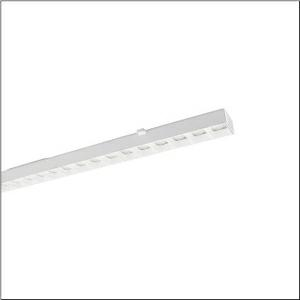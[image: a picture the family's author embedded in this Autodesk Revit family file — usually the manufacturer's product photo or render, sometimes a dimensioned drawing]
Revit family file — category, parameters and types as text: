
# Revit family: silica_r__31_fur_modario_r__31_51ry1tmb46c_60a4
name_source: partatom
category: Lighting Fixtures
units: mm (PartAtom-declared; Revit-internal decimal feet)

## family parameters
Cut with Voids When Loaded = No
Host = Face
Light Source = No
Part Type = Normal
Room Calculation Point = No
Round Connector Dimension = Use Diameter
Shared = No

## types (1)
- --- (1 x LED, 6710 lm, 37.8 W, 4000K)
    Apparent Load = 38 VA
    CIE Flux Codes = 84 98 100 100 100
    Color Rendering = 80
    Color Temperature = 4000K
    Default Elevation = 1800 mm
    Description = Silica® 31 for Modario® 31, luminaire insert, of aluminium, coated, traffic white (RAL 9016), length: 1.495mm, width: 79mm, height: 62mm, 5x system unit, system units: 299mm, LED rated luminous flux: 6.710lm, light colour: 840, control gear: ON/OFF Multilumen, with system connector: socket, mains connection: 220..240V, AC, 50/60Hz, rated input power: 38W, luminous flux adjustable on luminaire in four steps (3920/4730/5690/6710lm), connected load according to luminous flux setting (21.7/26.2/31.8/37.8W), primary light control with lens, of PMMA, primary anti-glare with reflector, of PC, CAT 2 (L<= 3000cd/m²), light emission: direct distribution, primary light characteristic: symmetric, protection rating (complete): IP20, insulation class (complete): insulation class I (protective earthing), certification: CE, UKCA, impact resistance: IK02, permissible ambient temperature for indoor applications: -20..+40°C, packaging unit: 1 piece
    Height = 62 mm  [stored 0.203412 ft]
    Lamp = 1 x LED
    Lamp Light Flux = 6710 lm
    Lamp Power = 37.8 W
    Lamp count = 1
    Length = 1495 mm
    Luminous efficacy = 178 lm/W
    Manufacturer = Siteco
    ModVariant = No
    Model = 51RY1TMB46C
    Mounting Place = Ceiling
    Mounting Type = Pendant
    Number of Poles = 1
    OnlyDefault = Yes
    Power Factor = 1
    Product Name = Silica® 31 für Modario® 31
    Product group = luminaire insert | ceiling pendant
    ProductGroupID = 902
    Protection Class = Protection class I
    Protection Degree = IP 20
    RLX_Detail_Level = 1
    RLX_Emergency_Light_Flux = 0 lm
    RLX_Emergency_Type = 0
    RLX_Emergency_Type_DB = No
    RlxData = <blob elided: 14069 chars, md5=0acf7f24>
    Socket = socket
    Standby Power = 0 W
    System Light Flux = 6710 lm
    System Power = 38 W
    Type Comments = factory setting: luminous flux: 100 % | (OFF | OFF | OFF) | 350 mA
    Type Image = l_1299352.jpg
    URL = http://relux.com
    VarID = @adj_078295
    Voltage = 0 V
    Weight = 0.00 kg
    Width = 79 mm

note: [stored X ft] marks values corroborated as IEEE doubles in the binary element streams (Revit-internal decimal feet)

## geometry (parser evidence)
native form markers: Sweep x14
no freeform markers — native parametric forms only
